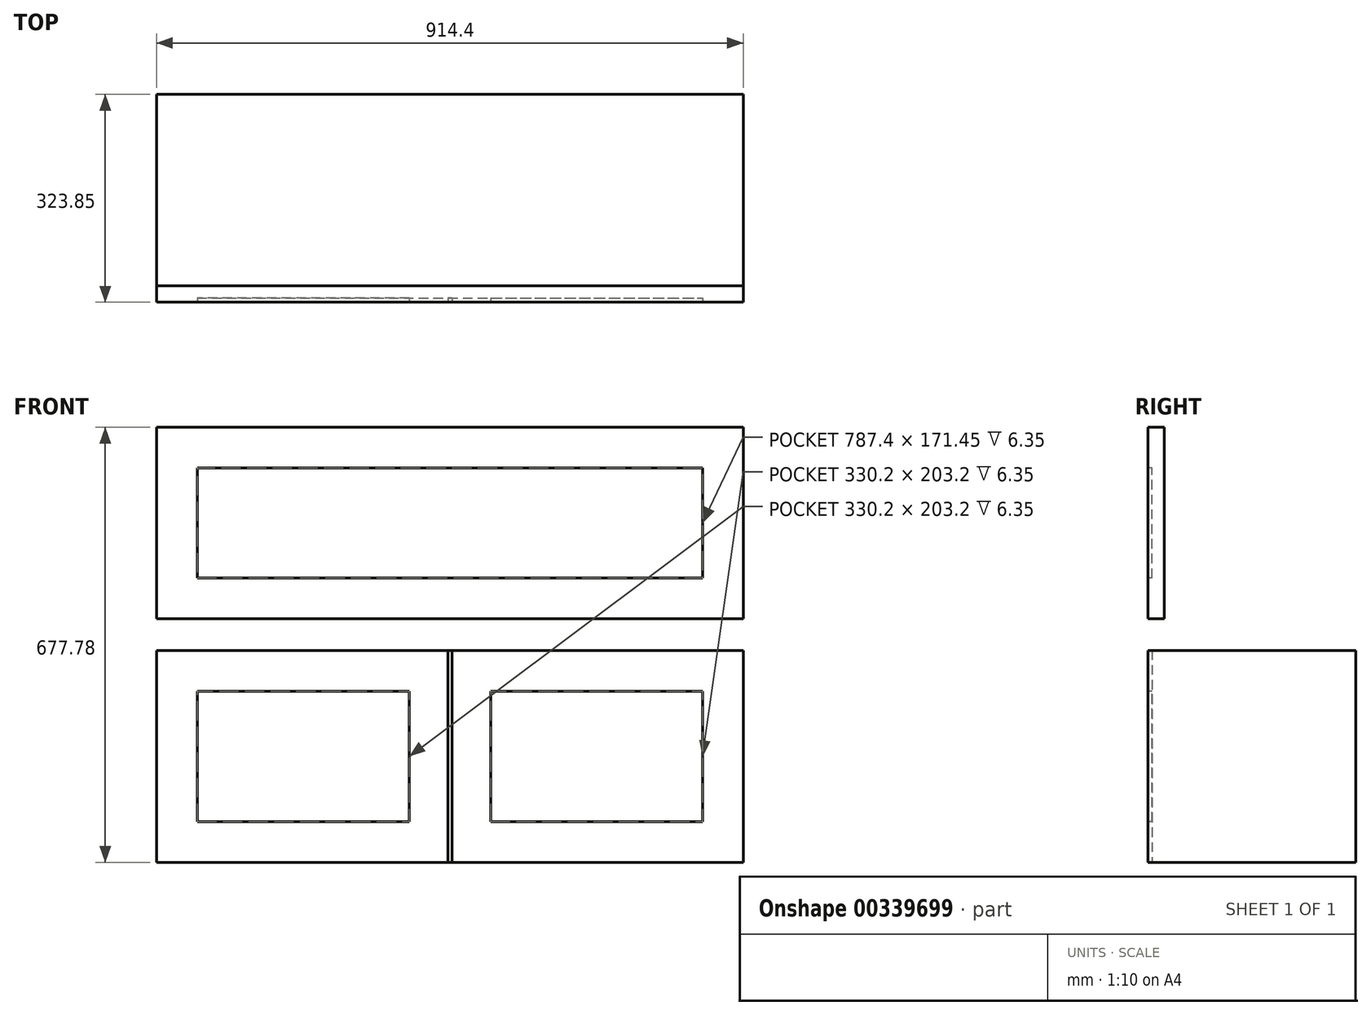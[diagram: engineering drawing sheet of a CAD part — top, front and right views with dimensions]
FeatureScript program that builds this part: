
annotation { "Feature Type Name" : "Feature", "Feature Type Description" : "" }
export const myFeature = defineFeature(function(context is Context, id is Id, definition is map)
    precondition{}
    {
        {
            var Q0;
            Q0=qCreatedBy(makeId("Front.planeOp"),FACE);
            var sketch = newSketch(context, id + "F0", { "sketchPlane" : qUnion([Q0])});
            skLineSegment(sketch, "E0.bottom", {"start": v(227.9, 0) * mm, "end": v(-229.3, 0) * mm});
            skLineSegment(sketch, "E0.top", {"start": v(227.9, 330.2) * mm, "end": v(-229.3, 330.2) * mm});
            skLineSegment(sketch, "E0.left", {"start": v(227.9, 0) * mm, "end": v(227.9, 330.2) * mm});
            skLineSegment(sketch, "E0.right", {"start": v(-229.3, 0) * mm, "end": v(-229.3, 330.2) * mm});
            skLineSegment(sketch, "E1.0", {"start": v(164.4, 266.7) * mm, "end": v(-165.8, 266.7) * mm});
            skLineSegment(sketch, "E1.1", {"start": v(164.4, 63.5) * mm, "end": v(164.4, 266.7) * mm});
            skLineSegment(sketch, "E1.2", {"start": v(164.4, 63.5) * mm, "end": v(-165.8, 63.5) * mm});
            skLineSegment(sketch, "E1.3", {"start": v(-165.8, 63.5) * mm, "end": v(-165.8, 266.7) * mm});
            skLineSegment(sketch, "E2.bottom", {"start": v(-229.3, 0) * mm, "end": v(227.9, 0) * mm});
            skLineSegment(sketch, "E3.bottom", {"start": v(-229.3, 330.2) * mm, "end": v(100.9, 330.2) * mm});
            skLineSegment(sketch, "E4.MirrorCS", {"start": v(227.9, 330.2) * mm, "end": v(685.1, 330.2) * mm});
            skLineSegment(sketch, "E5.MirrorCS", {"start": v(685.1, 330.2) * mm, "end": v(354.9, 330.2) * mm});
            skLineSegment(sketch, "E6.MirrorCS", {"start": v(227.9, 0) * mm, "end": v(685.1, 0) * mm});
            skLineSegment(sketch, "E7.MirrorCS", {"start": v(685.1, 0) * mm, "end": v(227.9, 0) * mm});
            skLineSegment(sketch, "E8.MirrorCS", {"start": v(621.6, 63.5) * mm, "end": v(621.6, 266.7) * mm});
            skLineSegment(sketch, "E9.MirrorCS", {"start": v(291.4, 63.5) * mm, "end": v(621.6, 63.5) * mm});
            skLineSegment(sketch, "E10.MirrorCS", {"start": v(291.4, 63.5) * mm, "end": v(291.4, 266.7) * mm});
            skLineSegment(sketch, "E11.MirrorCS", {"start": v(291.4, 266.7) * mm, "end": v(621.6, 266.7) * mm});
            skLineSegment(sketch, "E12.MirrorCS", {"start": v(685.1, 0) * mm, "end": v(685.1, 330.2) * mm});
            skLineSegment(sketch, "E13", {"start": v(224.73, 330.2) * mm, "end": v(224.73, 0) * mm});
            skLineSegment(sketch, "E14", {"start": v(231.08, 330.2) * mm, "end": v(231.08, 0) * mm});
            skLineSegment(sketch, "E15.bottom", {"start": v(-229.3, 379.33) * mm, "end": v(685.1, 379.33) * mm});
            skLineSegment(sketch, "E15.top", {"start": v(-229.3, 677.78) * mm, "end": v(685.1, 677.78) * mm});
            skLineSegment(sketch, "E15.left", {"start": v(-229.3, 379.33) * mm, "end": v(-229.3, 677.78) * mm});
            skLineSegment(sketch, "E15.right", {"start": v(685.1, 379.33) * mm, "end": v(685.1, 677.78) * mm});
            skLineSegment(sketch, "E16.0", {"start": v(-165.8, 614.28) * mm, "end": v(621.6, 614.28) * mm});
            skLineSegment(sketch, "E16.1", {"start": v(-165.8, 442.83) * mm, "end": v(-165.8, 614.28) * mm});
            skLineSegment(sketch, "E16.2", {"start": v(-165.8, 442.83) * mm, "end": v(621.6, 442.83) * mm});
            skLineSegment(sketch, "E16.3", {"start": v(621.6, 442.83) * mm, "end": v(621.6, 614.28) * mm});
            skSolve(sketch);
        }
        {
            var Q0;
            Q0=makeQuery(id+"F0.imprint","IMPRINT",FACE,{"disambiguationData":[TD([[makeQuery(id+"F0.imprint","IMPRINT",EDGE,{"derivedFrom":sQuery(id+"F0.wireOp",EDGE,"E1.0")}),1.0]])]});
            var Q1;
            Q1=makeQuery(id+"F0.imprint","IMPRINT",FACE,{"disambiguationData":[TD([[makeQuery(id+"F0.imprint","IMPRINT",EDGE,{"derivedFrom":sQuery(id+"F0.wireOp",EDGE,"E2.bottom")}),-1.0]])]});
            var Q2;
            Q2=makeQuery(id+"F0.imprint","IMPRINT",FACE,{"disambiguationData":[TD([[makeQuery(id+"F0.imprint","IMPRINT",EDGE,{"derivedFrom":sQuery(id+"F0.wireOp",EDGE,"E0.left")}),1.0]])]});
            var Q3;
            {var subQ0=sQuery(id+"F0.wireOp",EDGE,"E3.top");Q3=makeQuery(id+"F0.imprint","IMPRINT",FACE,{"disambiguationData":[TD([[makeQuery(id+"F0.imprint","IMPRINT",EDGE,{"derivedFrom":subQ0}),-1.0]])]});}
            var Q4;
            {var subQ0=sQuery(id+"F0.wireOp",EDGE,"E3.bottom");Q4=makeQuery(id+"F0.imprint","IMPRINT",FACE,{"disambiguationData":[TD([[makeQuery(id+"F0.imprint","IMPRINT",EDGE,{"derivedFrom":subQ0}),1.0]])]});}
            var Q5;
            Q5=makeQuery(id+"F0.imprint","IMPRINT",FACE,{"disambiguationData":[TD([[makeQuery(id+"F0.imprint","IMPRINT",EDGE,{"derivedFrom":sQuery(id+"F0.wireOp",EDGE,"E8.MirrorCS")}),1.0]])]});
            var Q6;
            {var subQ2=sQuery(id+"F0.wireOp",EDGE,"ed679ab7-f109-45c4-9ee2-0cc617b6c41517.MirrorCS");Q6=makeQuery(id+"F0.imprint","IMPRINT",FACE,{"disambiguationData":[TD([[makeQuery(id+"F0.imprint","IMPRINT",EDGE,{"derivedFrom":subQ2}),-1.0]])]});}
            var Q7;
            Q7=makeQuery(id+"F0.imprint","IMPRINT",FACE,{"disambiguationData":[TD([[makeQuery(id+"F0.imprint","IMPRINT",EDGE,{"derivedFrom":sQuery(id+"F0.wireOp",EDGE,"ed679ab7-f109-45c4-9ee2-0cc617b6c4156.MirrorCS")}),1.0]])]});
            var Q8;
            Q8=makeQuery(id+"F0.imprint","IMPRINT",FACE,{"disambiguationData":[TD([[makeQuery(id+"F0.imprint","IMPRINT",EDGE,{"derivedFrom":sQuery(id+"F0.wireOp",EDGE,"E0.left")}),-1.0]])]});
            var Q9;
            {var subQ0=sQuery(id+"F0.wireOp",EDGE,"E5.MirrorCS");Q9=makeQuery(id+"F0.imprint","IMPRINT",FACE,{"disambiguationData":[TD([[makeQuery(id+"F0.imprint","IMPRINT",EDGE,{"derivedFrom":subQ0}),-1.0]])]});}
            var Q10;
            {var subQ0=sQuery(id+"F0.wireOp",EDGE,"E0.right");Q10=makeQuery(id+"F0.imprint","IMPRINT",FACE,{"disambiguationData":[TD([[makeQuery(id+"F0.imprint","IMPRINT",EDGE,{"derivedFrom":subQ0}),-1.0]])]});}
            var Q11;
            Q11=makeQuery(id+"F0.imprint","IMPRINT",FACE,{"disambiguationData":[TD([[makeQuery(id+"F0.imprint","IMPRINT",EDGE,{"derivedFrom":sQuery(id+"F0.wireOp",EDGE,"E8.MirrorCS")}),-1.0]])]});
            extrude(context, id + "F1", {"entities" : qUnion([Q0, Q1, Q2, Q3, Q4, Q5, Q6, Q7, Q8, Q9, Q10, Q11]), "oppositeDirection" : true, "depth" : 323.85 * mm, "offsetDistance" : 25.4 * mm});
        }
        {
            var Q0;
            Q0=makeQuery(id+"F0.imprint","IMPRINT",FACE,{"disambiguationData":[TD([[makeQuery(id+"F0.imprint","IMPRINT",EDGE,{"derivedFrom":sQuery(id+"F0.wireOp",EDGE,"E1.0")}),1.0]])]});
            var Q1;
            Q1=makeQuery(id+"F0.imprint","IMPRINT",FACE,{"disambiguationData":[TD([[makeQuery(id+"F0.imprint","IMPRINT",EDGE,{"derivedFrom":sQuery(id+"F0.wireOp",EDGE,"E3.bottom")}),1.0]])]});
            var Q2;
            Q2=makeQuery(id+"F0.imprint","IMPRINT",FACE,{"disambiguationData":[TD([[makeQuery(id+"F0.imprint","IMPRINT",EDGE,{"derivedFrom":sQuery(id+"F0.wireOp",EDGE,"E8.MirrorCS")}),1.0]])]});
            var Q3;
            {var subQ0=sQuery(id+"F0.wireOp",EDGE,"E5.MirrorCS");Q3=makeQuery(id+"F0.imprint","IMPRINT",FACE,{"disambiguationData":[TD([[makeQuery(id+"F0.imprint","IMPRINT",EDGE,{"derivedFrom":subQ0}),-1.0]])]});}
            var Q4;
            {var subQ0=sQuery(id+"F0.wireOp",EDGE,"E0.left");Q4=makeQuery(id+"F0.imprint","IMPRINT",FACE,{"disambiguationData":[TD([[makeQuery(id+"F0.imprint","IMPRINT",EDGE,{"derivedFrom":subQ0}),1.0]])]});}
            var Q5;
            {var subQ0=sQuery(id+"F0.wireOp",EDGE,"E0.left");Q5=makeQuery(id+"F0.imprint","IMPRINT",FACE,{"disambiguationData":[TD([[makeQuery(id+"F0.imprint","IMPRINT",EDGE,{"derivedFrom":subQ0}),-1.0]])]});}
            extrude(context, id + "F2", {"entities" : qUnion([Q0, Q1, Q2, Q3, Q4, Q5]), "operationType" : NewBodyOperationType.REMOVE, "oppositeDirection" : true, "depth" : 6.35 * mm});
        }
        {
            var Q0;
            Q0=makeQuery(id+"F0.imprint","IMPRINT",FACE,{"disambiguationData":[TD([[makeQuery(id+"F0.imprint","IMPRINT",EDGE,{"derivedFrom":sQuery(id+"F0.wireOp",EDGE,"E15.bottom")}),1.0]])]});
            var Q1;
            Q1=makeQuery(id+"F0.imprint","IMPRINT",FACE,{"disambiguationData":[TD([[makeQuery(id+"F0.imprint","IMPRINT",EDGE,{"derivedFrom":sQuery(id+"F0.wireOp",EDGE,"E16.0")}),-1.0]])]});
            extrude(context, id + "F3", {"entities" : qUnion([Q0, Q1]), "oppositeDirection" : true, "depth" : 25.4 * mm});
        }
        {
            var Q0;
            Q0=makeQuery(id+"F0.imprint","IMPRINT",FACE,{"disambiguationData":[TD([[makeQuery(id+"F0.imprint","IMPRINT",EDGE,{"derivedFrom":sQuery(id+"F0.wireOp",EDGE,"E16.0")}),-1.0]])]});
            extrude(context, id + "F4", {"entities" : qUnion([Q0]), "operationType" : NewBodyOperationType.REMOVE, "oppositeDirection" : true, "depth" : 6.35 * mm});
        }
    });
